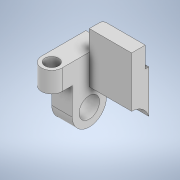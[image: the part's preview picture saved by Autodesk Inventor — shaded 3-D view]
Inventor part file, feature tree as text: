
AUTODESK INVENTOR PART (.ipt)
format: ipt  version: 2022 (Build 260153000, 153)  size: 156,672 bytes
history: native  units: mm
features: extrude x4, sketch x4
ambient origin geometry x8: Origin, YZ Plane, XZ Plane, XY Plane, X Axis, Y Axis, Z Axis, Center Point
bodies: Solid1 (feature_tree)
feature tree (8):
  extrude  "Extrusion1"  Depth=3.0mm
  extrude  "Extrusion2"  Depth=4.0mm
  extrude  "Extrusion3"  Depth=1.5mm
  extrude  "Extrusion4"  Depth=3.0mm TaperAngle=0.0deg
  sketch  "Sketch1"  dims[d4=2.0mm d5=3.0mm]
  sketch  "Sketch2"  dims[d8=8.0mm d9=4.0mm]
  sketch  "Sketch3"  dims[d10=1.5mm d11=1.5mm]
  sketch  "Sketch4"  dims[d12=2.5mm d13=3.0mm d14=0.0mm d15=2.0mm d16=1.0mm d17=0.5mm d18=3.0mm d19=0.0mm d20=5.0mm d21=3.0mm d22=2.5mm d23=4.0mm d24=3.0mm d25=0.0mm d26=5.2mm d27=3.0mm d28=0.0mm]
